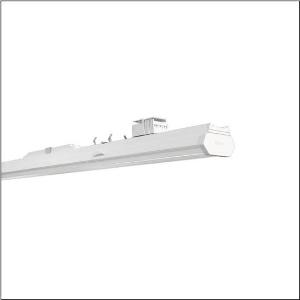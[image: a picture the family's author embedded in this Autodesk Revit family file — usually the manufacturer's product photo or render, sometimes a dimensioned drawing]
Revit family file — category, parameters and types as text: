
# Revit family: licross_r__11_protected_extreme_ho_51tp12dn4fxme_36ff
name_source: partatom
category: Lighting Fixtures
units: mm (PartAtom-declared; Revit-internal decimal feet)

## family parameters
Cut with Voids When Loaded = No
Host = Face
Light Source = No
Part Type = Normal
Room Calculation Point = No
Round Connector Dimension = Use Diameter
Shared = No

## types (1)
- --- (1 x LED, 15270 lm, 87.3 W, 4000K)
    Apparent Load = 87 VA
    CIE Flux Codes = 70 91 97 98 100
    Color Rendering = 80
    Color Temperature = 4000K
    Default Elevation = 1800 mm
    Description = Licross® 11 Protected extreme HO, luminaire insert, of sheet steel, galvanised, coil coated, white, length: 1.500mm, width: 90mm, height: 101mm, LED rated luminous flux: 15.270lm, light colour: 840, SDCM (Standard Deviation of Colour Matching)MacAdam ≤ 2 SDCM (initial), control gear: DALI 2, with plug, 5-pole, with phase selection, mains connection: 220..240V, AC, 50/60Hz, rated input power: 87W, internal wiring halogen-free, primary optical cover: cover, of PMMA, light emission: direct distribution, primary light characteristic: symmetric, protection rating (complete): IP64, insulation class (complete): insulation class I (protective earthing), certification: CE, ENEC, VDE, UKCA, protection symbol: D if used in an environment with conductive dust loads with corresponding accessories, impact resistance: IK06, permissible ambient temperature for indoor applications: -40..+40°C, corresponds to IFS (International Featured Standards) requirements for safety and quality in the food industry, reducing of maximum allowable ambient temperature of 5°C with ceiling mounting, LABS conformity tested according to VDMA 24364:2018-05, packaging unit: 1 piece
    Height = 92 mm
    Lamp = 1 x LED
    Lamp Light Flux = 15270 lm
    Lamp Power = 87.3 W
    Lamp count = 1
    Length = 1500 mm
    Luminous efficacy = 175 lm/W
    Manufacturer = Siteco
    ModVariant = No
    Model = 51TP12DN4FXME
    Mounting Place = Ceiling
    Mounting Type = Pendant
    Number of Poles = 1
    OnlyDefault = Yes
    Power Factor = 1
    Product Name = Licross® 11 Protected extreme HO
    Product group = luminaire insert | ceiling pendant
    ProductGroupID = 901
    Protection Class = Protection class I
    Protection Degree = IP 64
    RLX_Detail_Level = 1
    RLX_Emergency_Light_Flux = 0 lm
    RLX_Emergency_Type = 0
    RLX_Emergency_Type_DB = No
    RlxData = <blob elided: 24617 chars, md5=90f74f35>
    Socket = socket
    Standby Power = 0 W
    System Light Flux = 15270 lm
    System Power = 87 W
    Type Comments = factory setting: luminous flux: 100 % | dim-lin: 254 | 589 mA
    Type Image = l_1256148.jpg
    URL = http://relux.com
    VarID = @adj_090423
    Voltage = 0 V
    Weight = 0.00 kg
    Width = 88 mm

## geometry (parser evidence)
native form markers: Blend x4, Sweep x9
no freeform markers — native parametric forms only
